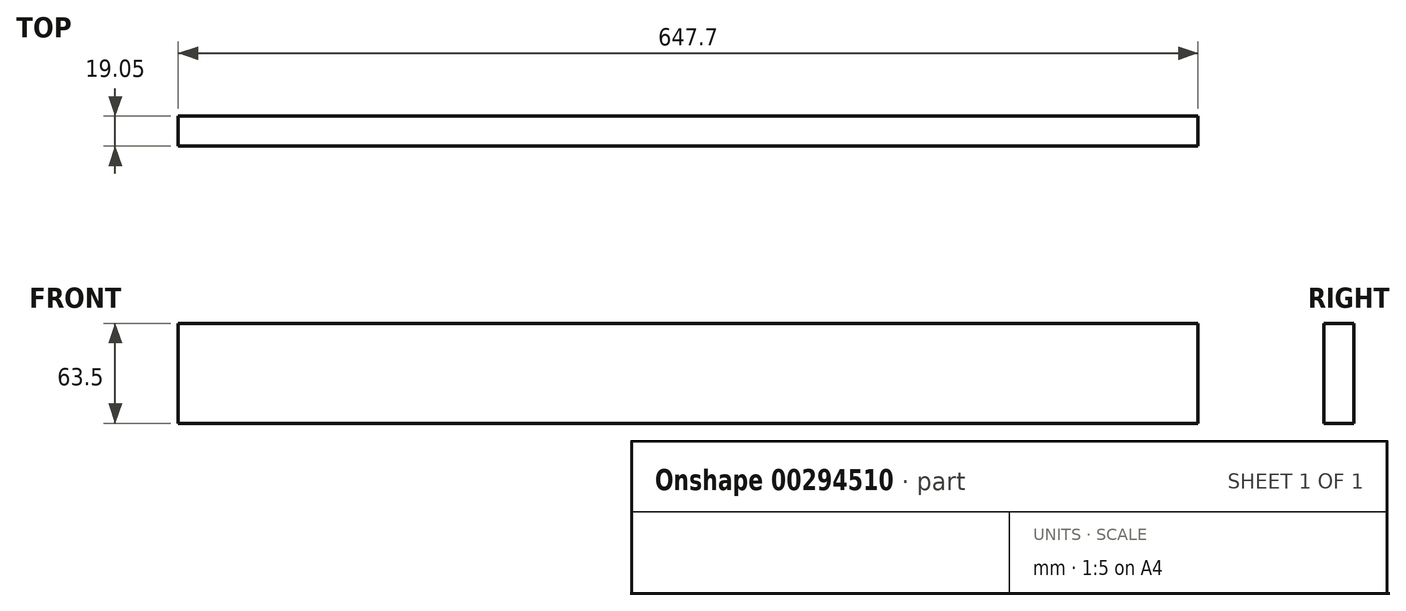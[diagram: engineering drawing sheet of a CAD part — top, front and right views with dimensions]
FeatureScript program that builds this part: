
annotation { "Feature Type Name" : "Feature", "Feature Type Description" : "" }
export const myFeature = defineFeature(function(context is Context, id is Id, definition is map)
    precondition{}
    {
        {
            var Q0;
            Q0=qCreatedBy(makeId("Front.planeOp"),FACE);
            var sketch = newSketch(context, id + "F0", { "sketchPlane" : qUnion([Q0])});
            skLineSegment(sketch, "E0.bottom", {"start": v(323.85, 31.75) * mm, "end": v(-323.85, 31.75) * mm});
            skLineSegment(sketch, "E0.top", {"start": v(323.85, -31.75) * mm, "end": v(-323.85, -31.75) * mm});
            skLineSegment(sketch, "E0.left", {"start": v(323.85, 31.75) * mm, "end": v(323.85, -31.75) * mm});
            skLineSegment(sketch, "E0.right", {"start": v(-323.85, 31.75) * mm, "end": v(-323.85, -31.75) * mm});
            skPoint(sketch, "E0.middle", {"position": v(0, 0) * mm});
            skSolve(sketch);
        }
        {
            var Q0;
            Q0=makeQuery(id+"F0.imprint","IMPRINT",FACE,{"disambiguationData":[TD([[makeQuery(id+"F0.imprint","IMPRINT",EDGE,{"derivedFrom":sQuery(id+"F0.wireOp",EDGE,"E0.bottom")}),1.0]])]});
            extrude(context, id + "F1", {"entities" : qUnion([Q0]), "depth" : 19.05 * mm});
        }
    });
